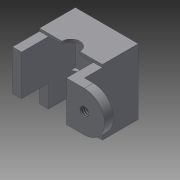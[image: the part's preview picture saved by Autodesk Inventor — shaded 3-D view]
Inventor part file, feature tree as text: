
AUTODESK INVENTOR PART (.ipt)
format: ipt  version: 2013 (Build 170138000, 138)  size: 145,920 bytes
history: native  units: mm
features: sketch x7, extrude x6, fillet x1, hole x1
ambient origin geometry x8: Origin, YZ Plane, XZ Plane, XY Plane, X Axis, Y Axis, Z Axis, Center Point
bodies: Solid1 (feature_tree)
feature tree (15):
  extrude  "Extrusion1"  Depth=12.0mm
  extrude  "Extrusion2"  Depth=2.0mm
  extrude  "Extrusion3"  Depth=0.6mm TaperAngle=0.0deg
  extrude  "Extrusion4"  Depth=5.0mm
  extrude  "Extrusion5"  Depth=5.0mm TaperAngle=0.0deg
  extrude  "Extrusion6"  Depth=5.0mm TaperAngle=0.0deg
  fillet  "Fillet1"  Radius=2.0mm
  hole  "Hole2"  [1 undecoded]
  sketch  "Sketch1"  dims[d0=10.0mm d2=12.0mm]
  sketch  "Sketch2"  dims[d3=2.0mm d4=2.0mm]
  sketch  "Sketch3"  dims[d5=9.0mm d6=0.0mm d7=0.6mm d8=0.0mm]
  sketch  "Sketch4"  dims[d9=5.0mm d10=0.0mm d11=5.0mm]
  sketch  "Sketch5"  dims[d14=12.0mm d15=5.0mm d16=0.0mm]
  sketch  "Sketch6"  dims[d17=4.0mm d18=5.0mm d19=0.0mm d20=2.0mm]
  sketch  "Sketch8"  dims[d22=6.5mm d23=0.0mm d32=4.5mm d33=2.013mm d34=6.0mm d35=4.0mm d36=2.0mm d37=90.0deg d38=8.0mm d39=20.594885mm]
note: 1 required parameter value undecoded (feature->parameter linkage not recoverable at this tier; creation-order binding heuristic only, values carry confidence <= 0.55)
